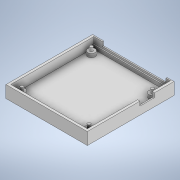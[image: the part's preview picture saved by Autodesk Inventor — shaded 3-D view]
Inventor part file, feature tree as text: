
AUTODESK INVENTOR PART (.ipt)
format: ipt  version: 2021 (Build 250183000, 183)  size: 284,160 bytes
history: native  units: mm
features: extrude x9, sketch x8, projected_geometry x2
ambient origin geometry x8: Origin, YZ Plane, XZ Plane, XY Plane, X Axis, Y Axis, Z Axis, Center Point
bodies: Solid1 (feature_tree)
feature tree (19):
  extrude  "Extrusion1"  Depth=62.0mm
  extrude  "Extrusion2"  Depth=3.0mm
  extrude  "Extrusion56"  Depth=3.0mm
  extrude  "Extrusion58"  Depth=4.5mm
  extrude  "Extrusion59"  Depth=3.0mm
  extrude  "Extrusion60"  Depth=54.35mm
  extrude  "Extrusion61"  Depth=51.56mm
  extrude  "Extrusion62"  Depth=6.0mm
  extrude  "Extrusion63"  Depth=6.0mm
  sketch  "Sketch2"  dims[d14=66.0mm d15=62.0mm]
  sketch  "Sketch69"  dims[d16=3.0mm d17=3.0mm]
  sketch  "Sketch72"  dims[d18=3.0mm d19=3.0mm]
  sketch  "Sketch73"  dims[d20=3.0mm d21=4.5mm]
  sketch  "Sketch74"  dims[d22=6.0mm d23=3.0mm]
  sketch  "Sketch75"  dims[d24=57.4mm d25=54.35mm]
  sketch  "Sketch77"  dims[d26=0.8mm d27=51.56mm]
  sketch  "Sketch78"  dims[d28=4.8mm d29=6.0mm d30=6.0mm d31=6.0mm d32=20.0mm d33=20.0mm d34=1.0mm d35=1.0mm d36=2.0mm d37=0.0mm d38=66.0mm d40=3.0mm d41=3.0mm d42=3.0mm d43=3.0mm d44=3.0mm d45=4.5mm d46=6.0mm d47=3.0mm d48=57.4mm d50=0.8mm d51=51.56mm d52=4.8mm d53=6.0mm d54=6.0mm d55=6.0mm d62=3.0mm d63=0.0mm d181=2.0mm d182=2.0mm d184=2.0mm d186=2.0mm d187=8.0mm d190=8.0mm d193=8.0mm d196=8.0mm d432=2.5mm d433=2.5mm d434=2.5mm d435=2.5mm d436=3.0mm d437=0.0mm d446=6.0mm d447=0.0mm d448=6.0mm d449=7.0mm d450=7.1mm d451=2.0mm d452=0.0mm d453=2.0mm d454=6.0mm d455=0.0mm d457=52.5mm d458=1.0mm d459=4.3mm d460=12.0mm d461=3.0mm d462=0.0mm d463=3.0mm d464=0.0mm d465=0.0mm d466=1.5mm d467=0.0mm d469=1.0mm d470=1.5mm d471=0.0mm d472=2.0mm d473=0.0mm d409=0.5mm d410=0.872665mm d411=0.5mm d412=0.872665mm d417=0.5mm d418=0.872665mm d419=0.5mm d420=0.872665mm]
  projected_geometry  "Projected Loop3"
  projected_geometry  "Projected Loop4"
